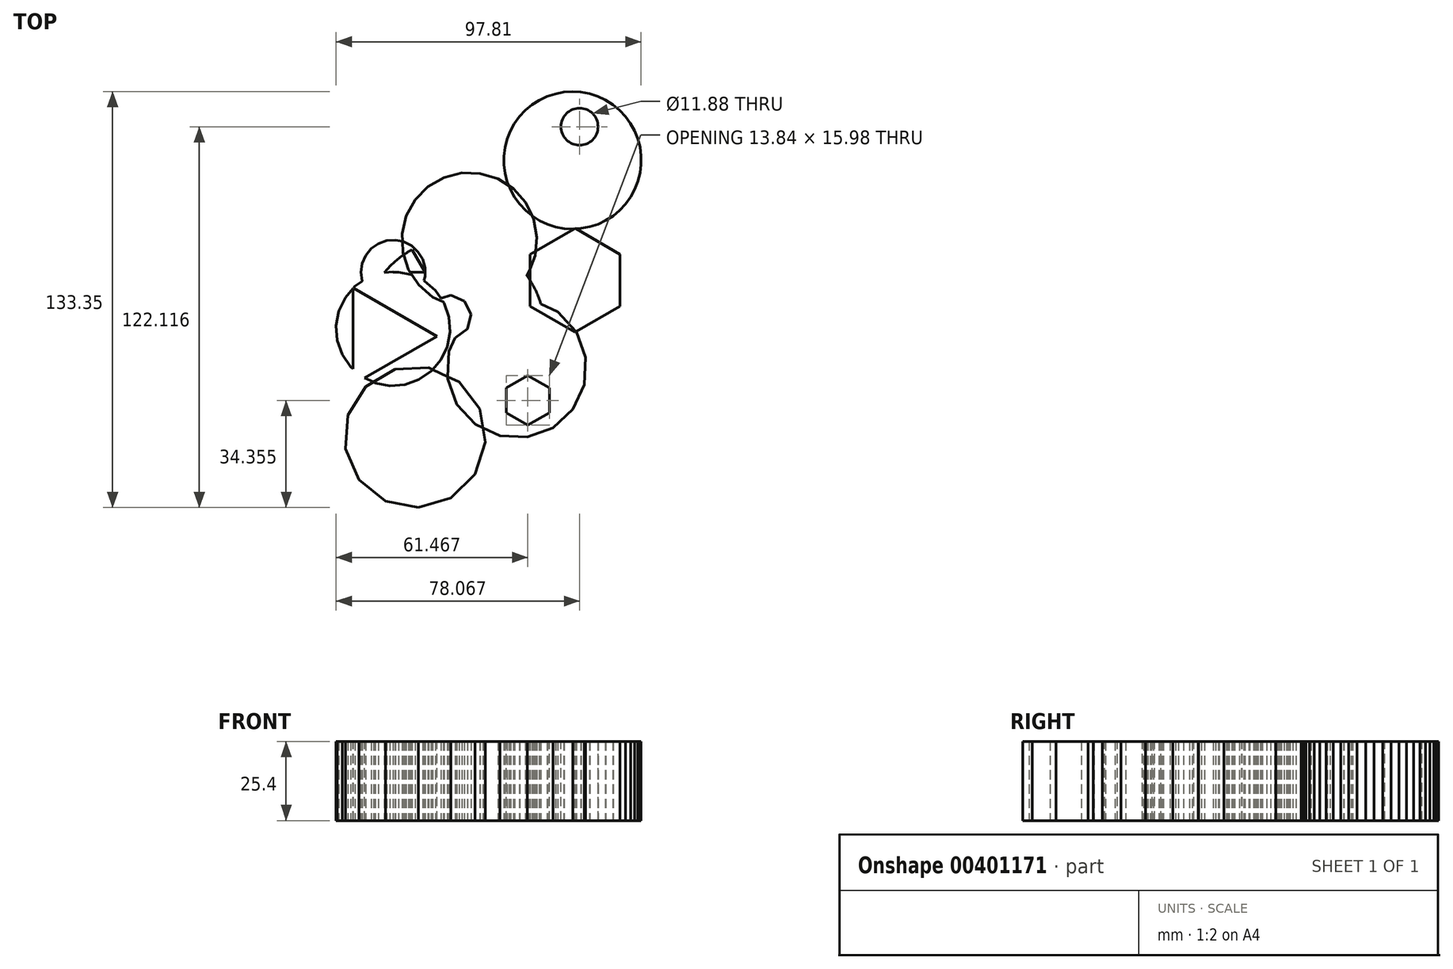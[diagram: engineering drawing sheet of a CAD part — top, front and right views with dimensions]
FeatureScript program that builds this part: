
annotation { "Feature Type Name" : "Feature", "Feature Type Description" : "" }
export const myFeature = defineFeature(function(context is Context, id is Id, definition is map)
    precondition{}
    {
        {
            var Q0;
            Q0=qCreatedBy(makeId("Top.planeOp"),FACE);
            var sketch = newSketch(context, id + "F0", { "sketchPlane" : qUnion([Q0])});
            skCircle(sketch, "E0", {"center": v(0, 0) * mm, "radius": 28.78 * mm});
            skCircle(sketch, "E1.cCircle", {"center": v(-14.58, 21.09) * mm, "radius": 2.96 * mm, "construction": true});
            skLineSegment(sketch, "E1.0", {"start": v(-9.46, 18.13) * mm, "end": v(-19.7, 18.13) * mm});
            skLineSegment(sketch, "E1.1", {"start": v(-19.7, 18.13) * mm, "end": v(-14.58, 27) * mm});
            skLineSegment(sketch, "E1.2", {"start": v(-14.58, 27) * mm, "end": v(-9.46, 18.13) * mm});
            skPoint(sketch, "E1.0.midPoint", {"position": v(-14.58, 18.13) * mm});
            skCircle(sketch, "E2.cCircle", {"center": v(-19.7, 18.13) * mm, "radius": 10.24 * mm, "construction": true});
            skLineSegment(sketch, "E2.0", {"start": v(-9.46, 19.54) * mm, "end": v(-9.46, 16.72) * mm});
            skLineSegment(sketch, "E2.1", {"start": v(-9.46, 16.72) * mm, "end": v(-10.22, 14.01) * mm});
            skLineSegment(sketch, "E2.2", {"start": v(-10.22, 14.01) * mm, "end": v(-11.69, 11.6) * mm});
            skLineSegment(sketch, "E2.3", {"start": v(-11.69, 11.6) * mm, "end": v(-13.74, 9.69) * mm});
            skLineSegment(sketch, "E2.4", {"start": v(-13.74, 9.69) * mm, "end": v(-16.24, 8.4) * mm});
            skLineSegment(sketch, "E2.5", {"start": v(-16.24, 8.4) * mm, "end": v(-19, 7.82) * mm});
            skLineSegment(sketch, "E2.6", {"start": v(-19, 7.82) * mm, "end": v(-21.8, 8.01) * mm});
            skLineSegment(sketch, "E2.7", {"start": v(-21.8, 8.01) * mm, "end": v(-24.46, 8.95) * mm});
            skLineSegment(sketch, "E2.8", {"start": v(-24.46, 8.95) * mm, "end": v(-26.76, 10.58) * mm});
            skLineSegment(sketch, "E2.9", {"start": v(-26.76, 10.58) * mm, "end": v(-28.53, 12.76) * mm});
            skLineSegment(sketch, "E2.10", {"start": v(-28.53, 12.76) * mm, "end": v(-29.66, 15.34) * mm});
            skLineSegment(sketch, "E2.11", {"start": v(-29.66, 15.34) * mm, "end": v(-30.04, 18.13) * mm});
            skLineSegment(sketch, "E2.12", {"start": v(-30.04, 18.13) * mm, "end": v(-29.66, 20.92) * mm});
            skLineSegment(sketch, "E2.13", {"start": v(-29.66, 20.92) * mm, "end": v(-28.53, 23.5) * mm});
            skLineSegment(sketch, "E2.14", {"start": v(-28.53, 23.5) * mm, "end": v(-26.76, 25.68) * mm});
            skLineSegment(sketch, "E2.15", {"start": v(-26.76, 25.68) * mm, "end": v(-24.46, 27.3) * mm});
            skLineSegment(sketch, "E2.16", {"start": v(-24.46, 27.3) * mm, "end": v(-21.8, 28.25) * mm});
            skLineSegment(sketch, "E2.17", {"start": v(-21.8, 28.25) * mm, "end": v(-19, 28.44) * mm});
            skLineSegment(sketch, "E2.18", {"start": v(-19, 28.44) * mm, "end": v(-16.24, 27.87) * mm});
            skLineSegment(sketch, "E2.19", {"start": v(-16.24, 27.87) * mm, "end": v(-13.74, 26.57) * mm});
            skLineSegment(sketch, "E2.20", {"start": v(-13.74, 26.57) * mm, "end": v(-11.69, 24.65) * mm});
            skLineSegment(sketch, "E2.21", {"start": v(-11.69, 24.65) * mm, "end": v(-10.22, 22.25) * mm});
            skLineSegment(sketch, "E2.22", {"start": v(-10.22, 22.25) * mm, "end": v(-9.46, 19.54) * mm});
            skPoint(sketch, "E2.0.midPoint", {"position": v(-9.46, 18.13) * mm});
            skCircle(sketch, "E3.cCircle", {"center": v(4.75, 28.39) * mm, "radius": 21.48 * mm, "construction": true});
            skLineSegment(sketch, "E3.0", {"start": v(15.55, 9.58) * mm, "end": v(10.07, 7.37) * mm});
            skLineSegment(sketch, "E3.1", {"start": v(10.07, 7.37) * mm, "end": v(4.2, 6.71) * mm});
            skLineSegment(sketch, "E3.2", {"start": v(4.2, 6.71) * mm, "end": v(-1.62, 7.66) * mm});
            skLineSegment(sketch, "E3.3", {"start": v(-1.62, 7.66) * mm, "end": v(-6.98, 10.15) * mm});
            skLineSegment(sketch, "E3.4", {"start": v(-6.98, 10.15) * mm, "end": v(-11.46, 14) * mm});
            skLineSegment(sketch, "E3.5", {"start": v(-11.46, 14) * mm, "end": v(-14.74, 18.9) * mm});
            skLineSegment(sketch, "E3.6", {"start": v(-14.74, 18.9) * mm, "end": v(-16.58, 24.52) * mm});
            skLineSegment(sketch, "E3.7", {"start": v(-16.58, 24.52) * mm, "end": v(-16.83, 30.42) * mm});
            skLineSegment(sketch, "E3.8", {"start": v(-16.83, 30.42) * mm, "end": v(-15.49, 36.17) * mm});
            skLineSegment(sketch, "E3.9", {"start": v(-15.49, 36.17) * mm, "end": v(-12.64, 41.34) * mm});
            skLineSegment(sketch, "E3.10", {"start": v(-12.64, 41.34) * mm, "end": v(-8.5, 45.55) * mm});
            skLineSegment(sketch, "E3.11", {"start": v(-8.5, 45.55) * mm, "end": v(-3.38, 48.49) * mm});
            skLineSegment(sketch, "E3.12", {"start": v(-3.38, 48.49) * mm, "end": v(2.35, 49.94) * mm});
            skLineSegment(sketch, "E3.13", {"start": v(2.35, 49.94) * mm, "end": v(8.25, 49.79) * mm});
            skLineSegment(sketch, "E3.14", {"start": v(8.25, 49.79) * mm, "end": v(13.9, 48.05) * mm});
            skLineSegment(sketch, "E3.15", {"start": v(13.9, 48.05) * mm, "end": v(18.86, 44.85) * mm});
            skLineSegment(sketch, "E3.16", {"start": v(18.86, 44.85) * mm, "end": v(22.78, 40.44) * mm});
            skLineSegment(sketch, "E3.17", {"start": v(22.78, 40.44) * mm, "end": v(25.36, 35.13) * mm});
            skLineSegment(sketch, "E3.18", {"start": v(25.36, 35.13) * mm, "end": v(26.42, 29.32) * mm});
            skLineSegment(sketch, "E3.19", {"start": v(26.42, 29.32) * mm, "end": v(25.87, 23.44) * mm});
            skLineSegment(sketch, "E3.20", {"start": v(25.87, 23.44) * mm, "end": v(23.75, 17.93) * mm});
            skLineSegment(sketch, "E3.21", {"start": v(23.75, 17.93) * mm, "end": v(20.22, 13.2) * mm});
            skLineSegment(sketch, "E3.22", {"start": v(20.22, 13.2) * mm, "end": v(15.55, 9.58) * mm});
            skPoint(sketch, "E3.0.midPoint", {"position": v(12.8, 8.47) * mm});
            skCircle(sketch, "E4.cCircle", {"center": v(-19.7, 0) * mm, "radius": 18.14 * mm, "construction": true});
            skLineSegment(sketch, "E4.0", {"start": v(-7.5, -13.63) * mm, "end": v(-11.43, -16.33) * mm});
            skLineSegment(sketch, "E4.1", {"start": v(-11.43, -16.33) * mm, "end": v(-15.94, -17.9) * mm});
            skLineSegment(sketch, "E4.2", {"start": v(-15.94, -17.9) * mm, "end": v(-20.7, -18.27) * mm});
            skLineSegment(sketch, "E4.3", {"start": v(-20.7, -18.27) * mm, "end": v(-25.4, -17.4) * mm});
            skLineSegment(sketch, "E4.4", {"start": v(-25.4, -17.4) * mm, "end": v(-29.7, -15.32) * mm});
            skLineSegment(sketch, "E4.5", {"start": v(-29.7, -15.32) * mm, "end": v(-33.33, -12.21) * mm});
            skLineSegment(sketch, "E4.6", {"start": v(-33.33, -12.21) * mm, "end": v(-36.03, -8.27) * mm});
            skLineSegment(sketch, "E4.7", {"start": v(-36.03, -8.27) * mm, "end": v(-37.61, -3.76) * mm});
            skLineSegment(sketch, "E4.8", {"start": v(-37.61, -3.76) * mm, "end": v(-37.98, 1) * mm});
            skLineSegment(sketch, "E4.9", {"start": v(-37.98, 1) * mm, "end": v(-37.1, 5.7) * mm});
            skLineSegment(sketch, "E4.10", {"start": v(-37.1, 5.7) * mm, "end": v(-35.03, 10) * mm});
            skLineSegment(sketch, "E4.11", {"start": v(-35.03, 10) * mm, "end": v(-31.91, 13.63) * mm});
            skLineSegment(sketch, "E4.12", {"start": v(-31.91, 13.63) * mm, "end": v(-27.97, 16.33) * mm});
            skLineSegment(sketch, "E4.13", {"start": v(-27.97, 16.33) * mm, "end": v(-23.46, 17.9) * mm});
            skLineSegment(sketch, "E4.14", {"start": v(-23.46, 17.9) * mm, "end": v(-18.7, 18.27) * mm});
            skLineSegment(sketch, "E4.15", {"start": v(-18.7, 18.27) * mm, "end": v(-14, 17.4) * mm});
            skLineSegment(sketch, "E4.16", {"start": v(-14, 17.4) * mm, "end": v(-9.7, 15.32) * mm});
            skLineSegment(sketch, "E4.17", {"start": v(-9.7, 15.32) * mm, "end": v(-6.07, 12.21) * mm});
            skLineSegment(sketch, "E4.18", {"start": v(-6.07, 12.21) * mm, "end": v(-3.38, 8.27) * mm});
            skLineSegment(sketch, "E4.19", {"start": v(-3.38, 8.27) * mm, "end": v(-1.8, 3.76) * mm});
            skLineSegment(sketch, "E4.20", {"start": v(-1.8, 3.76) * mm, "end": v(-1.43, -1) * mm});
            skLineSegment(sketch, "E4.21", {"start": v(-1.43, -1) * mm, "end": v(-2.31, -5.7) * mm});
            skLineSegment(sketch, "E4.22", {"start": v(-2.31, -5.7) * mm, "end": v(-4.38, -10) * mm});
            skLineSegment(sketch, "E4.23", {"start": v(-4.38, -10) * mm, "end": v(-7.5, -13.63) * mm});
            skPoint(sketch, "E4.0.midPoint", {"position": v(-9.46, -14.98) * mm});
            skCircle(sketch, "E5.cCircle", {"center": v(19.9, -12.61) * mm, "radius": 21.95 * mm, "construction": true});
            skPoint(sketch, "E5.cCircle.perimeterSnap0", {"position": v(-1.87, -3.35) * mm});
            skLineSegment(sketch, "E5.0", {"start": v(-1.84, -7.3) * mm, "end": v(1.84, 0.6) * mm});
            skLineSegment(sketch, "E5.1", {"start": v(1.84, 0.6) * mm, "end": v(8.28, 6.51) * mm});
            skLineSegment(sketch, "E5.2", {"start": v(8.28, 6.51) * mm, "end": v(16.48, 9.5) * mm});
            skLineSegment(sketch, "E5.3", {"start": v(16.48, 9.5) * mm, "end": v(25.2, 9.13) * mm});
            skLineSegment(sketch, "E5.4", {"start": v(25.2, 9.13) * mm, "end": v(33.13, 5.45) * mm});
            skLineSegment(sketch, "E5.5", {"start": v(33.13, 5.45) * mm, "end": v(39.03, -0.99) * mm});
            skLineSegment(sketch, "E5.6", {"start": v(39.03, -0.99) * mm, "end": v(42.02, -9.2) * mm});
            skLineSegment(sketch, "E5.7", {"start": v(42.02, -9.2) * mm, "end": v(41.65, -17.92) * mm});
            skLineSegment(sketch, "E5.8", {"start": v(41.65, -17.92) * mm, "end": v(37.97, -25.83) * mm});
            skLineSegment(sketch, "E5.9", {"start": v(37.97, -25.83) * mm, "end": v(31.53, -31.74) * mm});
            skLineSegment(sketch, "E5.10", {"start": v(31.53, -31.74) * mm, "end": v(23.33, -34.73) * mm});
            skLineSegment(sketch, "E5.11", {"start": v(23.33, -34.73) * mm, "end": v(14.6, -34.36) * mm});
            skLineSegment(sketch, "E5.12", {"start": v(14.6, -34.36) * mm, "end": v(6.68, -30.67) * mm});
            skLineSegment(sketch, "E5.13", {"start": v(6.68, -30.67) * mm, "end": v(0.78, -24.24) * mm});
            skLineSegment(sketch, "E5.14", {"start": v(0.78, -24.24) * mm, "end": v(-2.22, -16.03) * mm});
            skLineSegment(sketch, "E5.15", {"start": v(-2.22, -16.03) * mm, "end": v(-1.84, -7.3) * mm});
            skPoint(sketch, "E5.0.midPoint", {"position": v(0, -3.35) * mm});
            skPoint(sketch, "E5.0.midPoint.positionSnap0", {"position": v(-1.87, -3.35) * mm});
            skCircle(sketch, "E6.cCircle", {"center": v(-1.62, 3.76) * mm, "radius": 6.53 * mm, "construction": true});
            skLineSegment(sketch, "E6.0", {"start": v(3.13, 8.83) * mm, "end": v(5.28, 4.6) * mm});
            skLineSegment(sketch, "E6.1", {"start": v(5.28, 4.6) * mm, "end": v(4.2, -0.04) * mm});
            skLineSegment(sketch, "E6.2", {"start": v(4.2, -0.04) * mm, "end": v(0.4, -2.9) * mm});
            skLineSegment(sketch, "E6.3", {"start": v(0.4, -2.9) * mm, "end": v(-4.36, -2.63) * mm});
            skLineSegment(sketch, "E6.4", {"start": v(-4.36, -2.63) * mm, "end": v(-7.83, 0.62) * mm});
            skLineSegment(sketch, "E6.5", {"start": v(-7.83, 0.62) * mm, "end": v(-8.4, 5.34) * mm});
            skLineSegment(sketch, "E6.6", {"start": v(-8.4, 5.34) * mm, "end": v(-5.8, 9.32) * mm});
            skLineSegment(sketch, "E6.7", {"start": v(-5.8, 9.32) * mm, "end": v(-1.24, 10.7) * mm});
            skLineSegment(sketch, "E6.8", {"start": v(-1.24, 10.7) * mm, "end": v(3.13, 8.83) * mm});
            skPoint(sketch, "E6.0.midPoint", {"position": v(4.2, 6.71) * mm});
            skCircle(sketch, "E7.cCircle", {"center": v(38.63, 15.56) * mm, "radius": 14.4 * mm, "construction": true});
            skPoint(sketch, "E7.cCircle.centerSnap0", {"position": v(21.98, 15.56) * mm});
            skLineSegment(sketch, "E7.0", {"start": v(24.22, 7.24) * mm, "end": v(24.22, 23.88) * mm});
            skLineSegment(sketch, "E7.1", {"start": v(24.22, 23.88) * mm, "end": v(38.63, 32.2) * mm});
            skLineSegment(sketch, "E7.2", {"start": v(38.63, 32.2) * mm, "end": v(53.04, 23.88) * mm});
            skLineSegment(sketch, "E7.3", {"start": v(53.04, 23.88) * mm, "end": v(53.04, 7.24) * mm});
            skLineSegment(sketch, "E7.4", {"start": v(53.04, 7.24) * mm, "end": v(38.63, -1.08) * mm});
            skLineSegment(sketch, "E7.5", {"start": v(38.63, -1.08) * mm, "end": v(24.22, 7.24) * mm});
            skPoint(sketch, "E7.0.midPoint", {"position": v(24.22, 15.56) * mm});
            skCircle(sketch, "E8.cCircle", {"center": v(37.84, 54) * mm, "radius": 21.98 * mm, "construction": true});
            skLineSegment(sketch, "E8.0", {"start": v(35.14, 32.14) * mm, "end": v(32.42, 32.65) * mm});
            skLineSegment(sketch, "E8.1", {"start": v(32.42, 32.65) * mm, "end": v(29.79, 33.5) * mm});
            skLineSegment(sketch, "E8.2", {"start": v(29.79, 33.5) * mm, "end": v(27.28, 34.66) * mm});
            skLineSegment(sketch, "E8.3", {"start": v(27.28, 34.66) * mm, "end": v(24.94, 36.14) * mm});
            skLineSegment(sketch, "E8.4", {"start": v(24.94, 36.14) * mm, "end": v(22.8, 37.9) * mm});
            skLineSegment(sketch, "E8.5", {"start": v(22.8, 37.9) * mm, "end": v(20.9, 39.9) * mm});
            skLineSegment(sketch, "E8.6", {"start": v(20.9, 39.9) * mm, "end": v(19.27, 42.14) * mm});
            skLineSegment(sketch, "E8.7", {"start": v(19.27, 42.14) * mm, "end": v(17.93, 44.56) * mm});
            skLineSegment(sketch, "E8.8", {"start": v(17.93, 44.56) * mm, "end": v(16.9, 47.13) * mm});
            skLineSegment(sketch, "E8.9", {"start": v(16.9, 47.13) * mm, "end": v(16.21, 49.8) * mm});
            skLineSegment(sketch, "E8.10", {"start": v(16.21, 49.8) * mm, "end": v(15.86, 52.55) * mm});
            skLineSegment(sketch, "E8.11", {"start": v(15.86, 52.55) * mm, "end": v(15.85, 55.32) * mm});
            skLineSegment(sketch, "E8.12", {"start": v(15.85, 55.32) * mm, "end": v(16.19, 58.06) * mm});
            skLineSegment(sketch, "E8.13", {"start": v(16.19, 58.06) * mm, "end": v(16.87, 60.75) * mm});
            skLineSegment(sketch, "E8.14", {"start": v(16.87, 60.75) * mm, "end": v(17.88, 63.32) * mm});
            skLineSegment(sketch, "E8.15", {"start": v(17.88, 63.32) * mm, "end": v(19.2, 65.75) * mm});
            skLineSegment(sketch, "E8.16", {"start": v(19.2, 65.75) * mm, "end": v(20.83, 68) * mm});
            skLineSegment(sketch, "E8.17", {"start": v(20.83, 68) * mm, "end": v(22.71, 70.01) * mm});
            skLineSegment(sketch, "E8.18", {"start": v(22.71, 70.01) * mm, "end": v(24.84, 71.78) * mm});
            skLineSegment(sketch, "E8.19", {"start": v(24.84, 71.78) * mm, "end": v(27.17, 73.27) * mm});
            skLineSegment(sketch, "E8.20", {"start": v(27.17, 73.27) * mm, "end": v(29.67, 74.46) * mm});
            skLineSegment(sketch, "E8.21", {"start": v(29.67, 74.46) * mm, "end": v(32.3, 75.32) * mm});
            skLineSegment(sketch, "E8.22", {"start": v(32.3, 75.32) * mm, "end": v(35.02, 75.84) * mm});
            skLineSegment(sketch, "E8.23", {"start": v(35.02, 75.84) * mm, "end": v(37.78, 76.02) * mm});
            skLineSegment(sketch, "E8.24", {"start": v(37.78, 76.02) * mm, "end": v(40.54, 75.86) * mm});
            skLineSegment(sketch, "E8.25", {"start": v(40.54, 75.86) * mm, "end": v(43.26, 75.35) * mm});
            skLineSegment(sketch, "E8.26", {"start": v(43.26, 75.35) * mm, "end": v(45.89, 74.5) * mm});
            skLineSegment(sketch, "E8.27", {"start": v(45.89, 74.5) * mm, "end": v(48.4, 73.33) * mm});
            skLineSegment(sketch, "E8.28", {"start": v(48.4, 73.33) * mm, "end": v(50.73, 71.85) * mm});
            skLineSegment(sketch, "E8.29", {"start": v(50.73, 71.85) * mm, "end": v(52.87, 70.1) * mm});
            skLineSegment(sketch, "E8.30", {"start": v(52.87, 70.1) * mm, "end": v(54.77, 68.09) * mm});
            skLineSegment(sketch, "E8.31", {"start": v(54.77, 68.09) * mm, "end": v(56.4, 65.85) * mm});
            skLineSegment(sketch, "E8.32", {"start": v(56.4, 65.85) * mm, "end": v(57.74, 63.43) * mm});
            skLineSegment(sketch, "E8.33", {"start": v(57.74, 63.43) * mm, "end": v(58.77, 60.86) * mm});
            skLineSegment(sketch, "E8.34", {"start": v(58.77, 60.86) * mm, "end": v(59.46, 58.19) * mm});
            skLineSegment(sketch, "E8.35", {"start": v(59.46, 58.19) * mm, "end": v(59.82, 55.44) * mm});
            skLineSegment(sketch, "E8.36", {"start": v(59.82, 55.44) * mm, "end": v(59.83, 52.68) * mm});
            skLineSegment(sketch, "E8.37", {"start": v(59.83, 52.68) * mm, "end": v(59.49, 49.93) * mm});
            skLineSegment(sketch, "E8.38", {"start": v(59.49, 49.93) * mm, "end": v(58.8, 47.25) * mm});
            skLineSegment(sketch, "E8.39", {"start": v(58.8, 47.25) * mm, "end": v(57.8, 44.67) * mm});
            skLineSegment(sketch, "E8.40", {"start": v(57.8, 44.67) * mm, "end": v(56.47, 42.25) * mm});
            skLineSegment(sketch, "E8.41", {"start": v(56.47, 42.25) * mm, "end": v(54.85, 40) * mm});
            skLineSegment(sketch, "E8.42", {"start": v(54.85, 40) * mm, "end": v(52.96, 37.98) * mm});
            skLineSegment(sketch, "E8.43", {"start": v(52.96, 37.98) * mm, "end": v(50.83, 36.21) * mm});
            skLineSegment(sketch, "E8.44", {"start": v(50.83, 36.21) * mm, "end": v(48.5, 34.72) * mm});
            skLineSegment(sketch, "E8.45", {"start": v(48.5, 34.72) * mm, "end": v(46, 33.54) * mm});
            skLineSegment(sketch, "E8.46", {"start": v(46, 33.54) * mm, "end": v(43.38, 32.68) * mm});
            skLineSegment(sketch, "E8.47", {"start": v(43.38, 32.68) * mm, "end": v(40.66, 32.15) * mm});
            skLineSegment(sketch, "E8.48", {"start": v(40.66, 32.15) * mm, "end": v(37.9, 31.97) * mm});
            skLineSegment(sketch, "E8.49", {"start": v(37.9, 31.97) * mm, "end": v(35.14, 32.14) * mm});
            skPoint(sketch, "E8.0.midPoint", {"position": v(33.78, 32.4) * mm});
            skCircle(sketch, "E9.cCircle", {"center": v(-12.64, -34.73) * mm, "radius": 21.96 * mm, "construction": true});
            skLineSegment(sketch, "E9.0", {"start": v(-8.29, -12.54) * mm, "end": v(1.53, -17.1) * mm});
            skLineSegment(sketch, "E9.1", {"start": v(1.53, -17.1) * mm, "end": v(8.1, -25.7) * mm});
            skLineSegment(sketch, "E9.2", {"start": v(8.1, -25.7) * mm, "end": v(9.92, -36.38) * mm});
            skLineSegment(sketch, "E9.3", {"start": v(9.92, -36.38) * mm, "end": v(6.58, -46.67) * mm});
            skLineSegment(sketch, "E9.4", {"start": v(6.58, -46.67) * mm, "end": v(-1.17, -54.23) * mm});
            skLineSegment(sketch, "E9.5", {"start": v(-1.17, -54.23) * mm, "end": v(-11.55, -57.33) * mm});
            skLineSegment(sketch, "E9.6", {"start": v(-11.55, -57.33) * mm, "end": v(-22.17, -55.24) * mm});
            skLineSegment(sketch, "E9.7", {"start": v(-22.17, -55.24) * mm, "end": v(-30.61, -48.46) * mm});
            skLineSegment(sketch, "E9.8", {"start": v(-30.61, -48.46) * mm, "end": v(-34.93, -38.54) * mm});
            skLineSegment(sketch, "E9.9", {"start": v(-34.93, -38.54) * mm, "end": v(-34.15, -27.74) * mm});
            skLineSegment(sketch, "E9.10", {"start": v(-34.15, -27.74) * mm, "end": v(-28.43, -18.54) * mm});
            skLineSegment(sketch, "E9.11", {"start": v(-28.43, -18.54) * mm, "end": v(-19.1, -13.06) * mm});
            skLineSegment(sketch, "E9.12", {"start": v(-19.1, -13.06) * mm, "end": v(-8.29, -12.54) * mm});
            skPoint(sketch, "E9.0.midPoint", {"position": v(-3.38, -14.82) * mm});
            skCircle(sketch, "E10.cCircle", {"center": v(41.91, 66.19) * mm, "radius": 4.58 * mm, "construction": true});
            skPoint(sketch, "E10.0.midPoint", {"position": v(45.12, 62.92) * mm});
            skSolve(sketch);
        }
        {
            var Q0;
            {var subQ4=sQuery(id+"F0.wireOp",EDGE,"E3.16");Q0=makeQuery(id+"F0.imprint","IMPRINT",FACE,{"disambiguationData":[TD([[makeQuery(id+"F0.imprint","IMPRINT",EDGE,{"derivedFrom":subQ4}),1.0]])]});}
            var Q1;
            {var subQ6=sQuery(id+"F0.wireOp",EDGE,"E2.21");Q1=makeQuery(id+"F0.imprint","IMPRINT",FACE,{"disambiguationData":[TD([[makeQuery(id+"F0.imprint","IMPRINT",EDGE,{"derivedFrom":subQ6}),1.0]])]});}
            var Q2;
            {var subQ1=sQuery(id+"F0.wireOp",EDGE,"E7.3");Q2=makeQuery(id+"F0.imprint","IMPRINT",FACE,{"disambiguationData":[TD([[makeQuery(id+"F0.imprint","IMPRINT",EDGE,{"derivedFrom":subQ1}),-1.0]])]});}
            var Q3;
            {var subQ21=sQuery(id+"F0.wireOp",EDGE,"E2.19");Q3=makeQuery(id+"F0.imprint","IMPRINT",FACE,{"disambiguationData":[TD([[makeQuery(id+"F0.imprint","IMPRINT",EDGE,{"derivedFrom":subQ21}),1.0]])]});}
            var Q4;
            {var subQ12=sQuery(id+"F0.wireOp",EDGE,"E2.11");Q4=makeQuery(id+"F0.imprint","IMPRINT",FACE,{"disambiguationData":[TD([[makeQuery(id+"F0.imprint","IMPRINT",EDGE,{"derivedFrom":subQ12}),-1.0]])]});}
            var Q5;
            {var subQ5=sQuery(id+"F0.wireOp",EDGE,"E4.5");Q5=makeQuery(id+"F0.imprint","IMPRINT",FACE,{"disambiguationData":[TD([[makeQuery(id+"F0.imprint","IMPRINT",EDGE,{"derivedFrom":subQ5}),-1.0]])]});}
            var Q6;
            {var subQ15=sQuery(id+"F0.wireOp",EDGE,"E2.3");Q6=makeQuery(id+"F0.imprint","IMPRINT",FACE,{"disambiguationData":[TD([[makeQuery(id+"F0.imprint","IMPRINT",EDGE,{"derivedFrom":subQ15}),1.0]])]});}
            var Q7;
            {var subQ6=sQuery(id+"F0.wireOp",EDGE,"E2.3");Q7=makeQuery(id+"F0.imprint","IMPRINT",FACE,{"disambiguationData":[TD([[makeQuery(id+"F0.imprint","IMPRINT",EDGE,{"derivedFrom":subQ6}),-1.0]])]});}
            var Q8;
            {var subQ5=sQuery(id+"F0.wireOp",EDGE,"E1.2");var subQ7=sQuery(id+"F0.wireOp",EDGE,"E0");var subQ8=makeQuery(id+"F0.imprint","INTERSECT",VERTEX,{"derivedFrom":[subQ7,subQ5]});Q8=makeQuery(id+"F0.imprint","IMPRINT",FACE,{"disambiguationData":[TD([[makeQuery(id+"F0.imprint","IMPRINT",EDGE,{"disambiguationData":[TD([[subQ8,-1.0]])],"derivedFrom":subQ7}),1.0]])]});}
            var Q9;
            {var subQ5=sQuery(id+"F0.wireOp",EDGE,"E9.3");Q9=makeQuery(id+"F0.imprint","IMPRINT",FACE,{"disambiguationData":[TD([[makeQuery(id+"F0.imprint","IMPRINT",EDGE,{"derivedFrom":subQ5}),-1.0]])]});}
            var Q10;
            {var subQ12=sQuery(id+"F0.wireOp",EDGE,"E5.6");Q10=makeQuery(id+"F0.imprint","IMPRINT",FACE,{"disambiguationData":[TD([[makeQuery(id+"F0.imprint","IMPRINT",EDGE,{"derivedFrom":subQ12}),-1.0]])]});}
            var Q11;
            {var subQ9=sQuery(id+"F0.wireOp",EDGE,"E4.0");Q11=makeQuery(id+"F0.imprint","IMPRINT",FACE,{"disambiguationData":[TD([[makeQuery(id+"F0.imprint","IMPRINT",EDGE,{"derivedFrom":subQ9}),1.0]])]});}
            var Q12;
            {var subQ11=sQuery(id+"F0.wireOp",EDGE,"E5.2");Q12=makeQuery(id+"F0.imprint","IMPRINT",FACE,{"disambiguationData":[TD([[makeQuery(id+"F0.imprint","IMPRINT",EDGE,{"derivedFrom":subQ11}),-1.0]])]});}
            var Q13;
            {var subQ1=sQuery(id+"F0.wireOp",EDGE,"E4.19");Q13=makeQuery(id+"F0.imprint","IMPRINT",FACE,{"disambiguationData":[TD([[makeQuery(id+"F0.imprint","IMPRINT",EDGE,{"derivedFrom":subQ1}),-1.0]])]});}
            var Q14;
            Q14=makeQuery(id+"F0.imprint","IMPRINT",FACE,{"disambiguationData":[TD([[makeQuery(id+"F0.imprint","IMPRINT",EDGE,{"derivedFrom":sQuery(id+"F0.wireOp",EDGE,"E3.0")}),1.0]])]});
            var Q15;
            {var subQ0=sQuery(id+"F0.wireOp",EDGE,"E4.13");Q15=makeQuery(id+"F0.imprint","IMPRINT",FACE,{"disambiguationData":[TD([[makeQuery(id+"F0.imprint","IMPRINT",EDGE,{"derivedFrom":subQ0}),-1.0]])]});}
            extrude(context, id + "F1", {"entities" : qUnion([Q0, Q1, Q2, Q3, Q4, Q5, Q6, Q7, Q8, Q9, Q10, Q11, Q12, Q13, Q14, Q15]), "depth" : 25.4 * mm});
        }
        {
            var Q0;
            Q0=makeQuery(id+"F1.opExtrude","CAP_FACE",FACE,{"disambiguationData":[OSD([sQuery(id+"F0.wireOp",EDGE,"E3.15"),sQuery(id+"F0.wireOp",EDGE,"E3.16"),sQuery(id+"F0.wireOp",EDGE,"E3.17"),sQuery(id+"F0.wireOp",EDGE,"E7.1"),sQuery(id+"F0.wireOp",EDGE,"E7.2"),sQuery(id+"F0.wireOp",EDGE,"E8.0"),sQuery(id+"F0.wireOp",EDGE,"E8.1"),sQuery(id+"F0.wireOp",EDGE,"E8.2"),sQuery(id+"F0.wireOp",EDGE,"E8.3"),sQuery(id+"F0.wireOp",EDGE,"E8.4"),sQuery(id+"F0.wireOp",EDGE,"E8.8"),sQuery(id+"F0.wireOp",EDGE,"E8.9"),sQuery(id+"F0.wireOp",EDGE,"E8.10"),sQuery(id+"F0.wireOp",EDGE,"E8.11"),sQuery(id+"F0.wireOp",EDGE,"E8.12"),sQuery(id+"F0.wireOp",EDGE,"E8.13"),sQuery(id+"F0.wireOp",EDGE,"E8.14"),sQuery(id+"F0.wireOp",EDGE,"E8.15"),sQuery(id+"F0.wireOp",EDGE,"E8.16"),sQuery(id+"F0.wireOp",EDGE,"E8.17"),sQuery(id+"F0.wireOp",EDGE,"E8.18"),sQuery(id+"F0.wireOp",EDGE,"E8.19"),sQuery(id+"F0.wireOp",EDGE,"E8.20"),sQuery(id+"F0.wireOp",EDGE,"E8.21"),sQuery(id+"F0.wireOp",EDGE,"E8.22"),sQuery(id+"F0.wireOp",EDGE,"E8.23"),sQuery(id+"F0.wireOp",EDGE,"E8.24"),sQuery(id+"F0.wireOp",EDGE,"E8.25"),sQuery(id+"F0.wireOp",EDGE,"E8.26"),sQuery(id+"F0.wireOp",EDGE,"E8.27"),sQuery(id+"F0.wireOp",EDGE,"E8.28"),sQuery(id+"F0.wireOp",EDGE,"E8.29"),sQuery(id+"F0.wireOp",EDGE,"E8.30"),sQuery(id+"F0.wireOp",EDGE,"E8.31"),sQuery(id+"F0.wireOp",EDGE,"E8.32"),sQuery(id+"F0.wireOp",EDGE,"E8.33"),sQuery(id+"F0.wireOp",EDGE,"E8.34"),sQuery(id+"F0.wireOp",EDGE,"E8.35"),sQuery(id+"F0.wireOp",EDGE,"E8.36"),sQuery(id+"F0.wireOp",EDGE,"E8.37"),sQuery(id+"F0.wireOp",EDGE,"E8.38"),sQuery(id+"F0.wireOp",EDGE,"E8.39"),sQuery(id+"F0.wireOp",EDGE,"E8.40"),sQuery(id+"F0.wireOp",EDGE,"E8.41"),sQuery(id+"F0.wireOp",EDGE,"E8.42"),sQuery(id+"F0.wireOp",EDGE,"E8.43"),sQuery(id+"F0.wireOp",EDGE,"E8.44"),sQuery(id+"F0.wireOp",EDGE,"E8.45"),sQuery(id+"F0.wireOp",EDGE,"E8.46"),sQuery(id+"F0.wireOp",EDGE,"E8.47"),sQuery(id+"F0.wireOp",EDGE,"E8.48"),sQuery(id+"F0.wireOp",EDGE,"E8.49")])],"isStart":false});
            var sketch = newSketch(context, id + "F2", { "sketchPlane" : qUnion([Q0])});
            skCircle(sketch, "E11", {"center": v(40.09, 64.79) * mm, "radius": 5.94 * mm});
            skSolve(sketch);
        }
        {
            var Q0;
            Q0 = qSketchRegion(id + "F2", true);
            extrude(context, id + "F3", {"entities" : qUnion([Q0]), "operationType" : NewBodyOperationType.REMOVE, "endBound" : BoundingType.THROUGH_ALL, "oppositeDirection" : true, "depth" : 25.4 * mm});
        }
        {
            var Q0;
            Q0=makeQuery(id+"F1.opExtrude","CAP_FACE",FACE,{"disambiguationData":[OSD([sQuery(id+"F0.wireOp",EDGE,"E0"),sQuery(id+"F0.wireOp",EDGE,"E2.0"),sQuery(id+"F0.wireOp",EDGE,"E2.1"),sQuery(id+"F0.wireOp",EDGE,"E2.18"),sQuery(id+"F0.wireOp",EDGE,"E2.19"),sQuery(id+"F0.wireOp",EDGE,"E2.20"),sQuery(id+"F0.wireOp",EDGE,"E2.21"),sQuery(id+"F0.wireOp",EDGE,"E2.22"),sQuery(id+"F0.wireOp",EDGE,"E3.7"),sQuery(id+"F0.wireOp",EDGE,"E3.8"),sQuery(id+"F0.wireOp",EDGE,"E3.9"),sQuery(id+"F0.wireOp",EDGE,"E3.10"),sQuery(id+"F0.wireOp",EDGE,"E3.11"),sQuery(id+"F0.wireOp",EDGE,"E3.12"),sQuery(id+"F0.wireOp",EDGE,"E3.13"),sQuery(id+"F0.wireOp",EDGE,"E3.14"),sQuery(id+"F0.wireOp",EDGE,"E3.15"),sQuery(id+"F0.wireOp",EDGE,"E3.17"),sQuery(id+"F0.wireOp",EDGE,"E3.18"),sQuery(id+"F0.wireOp",EDGE,"E3.19"),sQuery(id+"F0.wireOp",EDGE,"E3.20"),sQuery(id+"F0.wireOp",EDGE,"E3.21"),sQuery(id+"F0.wireOp",EDGE,"E4.16"),sQuery(id+"F0.wireOp",EDGE,"E4.17"),sQuery(id+"F0.wireOp",EDGE,"E4.18"),sQuery(id+"F0.wireOp",EDGE,"E5.0"),sQuery(id+"F0.wireOp",EDGE,"E5.5"),sQuery(id+"F0.wireOp",EDGE,"E5.6"),sQuery(id+"F0.wireOp",EDGE,"E5.7"),sQuery(id+"F0.wireOp",EDGE,"E5.8"),sQuery(id+"F0.wireOp",EDGE,"E5.9"),sQuery(id+"F0.wireOp",EDGE,"E5.10"),sQuery(id+"F0.wireOp",EDGE,"E5.11"),sQuery(id+"F0.wireOp",EDGE,"E5.12"),sQuery(id+"F0.wireOp",EDGE,"E5.15"),sQuery(id+"F0.wireOp",EDGE,"E6.0"),sQuery(id+"F0.wireOp",EDGE,"E6.1"),sQuery(id+"F0.wireOp",EDGE,"E6.2"),sQuery(id+"F0.wireOp",EDGE,"E6.3"),sQuery(id+"F0.wireOp",EDGE,"E6.7"),sQuery(id+"F0.wireOp",EDGE,"E6.8"),sQuery(id+"F0.wireOp",EDGE,"E7.0"),sQuery(id+"F0.wireOp",EDGE,"E7.1"),sQuery(id+"F0.wireOp",EDGE,"E7.4"),sQuery(id+"F0.wireOp",EDGE,"E7.5"),sQuery(id+"F0.wireOp",EDGE,"E8.4"),sQuery(id+"F0.wireOp",EDGE,"E8.5"),sQuery(id+"F0.wireOp",EDGE,"E8.6"),sQuery(id+"F0.wireOp",EDGE,"E8.7"),sQuery(id+"F0.wireOp",EDGE,"E8.8"),sQuery(id+"F0.wireOp",EDGE,"E9.0"),sQuery(id+"F0.wireOp",EDGE,"E9.1"),sQuery(id+"F0.wireOp",EDGE,"E9.2")])],"isStart":false});
            var sketch = newSketch(context, id + "F4", { "sketchPlane" : qUnion([Q0])});
            skCircle(sketch, "E12.cCircle", {"center": v(23.49, -22.97) * mm, "radius": 6.92 * mm, "construction": true});
            skLineSegment(sketch, "E12.0", {"start": v(30.4, -18.98) * mm, "end": v(30.4, -26.97) * mm});
            skLineSegment(sketch, "E12.1", {"start": v(30.4, -26.97) * mm, "end": v(23.49, -30.96) * mm});
            skLineSegment(sketch, "E12.2", {"start": v(23.49, -30.96) * mm, "end": v(16.57, -26.97) * mm});
            skLineSegment(sketch, "E12.3", {"start": v(16.57, -26.97) * mm, "end": v(16.57, -18.98) * mm});
            skLineSegment(sketch, "E12.4", {"start": v(16.57, -18.98) * mm, "end": v(23.49, -14.99) * mm});
            skLineSegment(sketch, "E12.5", {"start": v(23.49, -14.99) * mm, "end": v(30.4, -18.98) * mm});
            skPoint(sketch, "E12.0.midPoint", {"position": v(30.4, -22.97) * mm});
            skSolve(sketch);
        }
        {
            var Q0;
            Q0 = qSketchRegion(id + "F4", true);
            extrude(context, id + "F5", {"entities" : qUnion([Q0]), "operationType" : NewBodyOperationType.REMOVE, "endBound" : BoundingType.THROUGH_ALL, "oppositeDirection" : true, "depth" : 25.4 * mm});
        }
        {
            var Q0;
            Q0=makeQuery(id+"F1.opExtrude","CAP_FACE",FACE,{"disambiguationData":[OSD([sQuery(id+"F0.wireOp",EDGE,"E0"),sQuery(id+"F0.wireOp",EDGE,"E1.0"),sQuery(id+"F0.wireOp",EDGE,"E1.1"),sQuery(id+"F0.wireOp",EDGE,"E2.10"),sQuery(id+"F0.wireOp",EDGE,"E2.11"),sQuery(id+"F0.wireOp",EDGE,"E2.12"),sQuery(id+"F0.wireOp",EDGE,"E2.13"),sQuery(id+"F0.wireOp",EDGE,"E2.14"),sQuery(id+"F0.wireOp",EDGE,"E2.15"),sQuery(id+"F0.wireOp",EDGE,"E2.16"),sQuery(id+"F0.wireOp",EDGE,"E2.17"),sQuery(id+"F0.wireOp",EDGE,"E2.18"),sQuery(id+"F0.wireOp",EDGE,"E3.3"),sQuery(id+"F0.wireOp",EDGE,"E3.4"),sQuery(id+"F0.wireOp",EDGE,"E3.5"),sQuery(id+"F0.wireOp",EDGE,"E3.6"),sQuery(id+"F0.wireOp",EDGE,"E3.7"),sQuery(id+"F0.wireOp",EDGE,"E4.4"),sQuery(id+"F0.wireOp",EDGE,"E4.5"),sQuery(id+"F0.wireOp",EDGE,"E4.6"),sQuery(id+"F0.wireOp",EDGE,"E4.7"),sQuery(id+"F0.wireOp",EDGE,"E4.8"),sQuery(id+"F0.wireOp",EDGE,"E4.9"),sQuery(id+"F0.wireOp",EDGE,"E4.10"),sQuery(id+"F0.wireOp",EDGE,"E4.11"),sQuery(id+"F0.wireOp",EDGE,"E4.12"),sQuery(id+"F0.wireOp",EDGE,"E4.14"),sQuery(id+"F0.wireOp",EDGE,"E4.15"),sQuery(id+"F0.wireOp",EDGE,"E4.16"),sQuery(id+"F0.wireOp",EDGE,"E4.18"),sQuery(id+"F0.wireOp",EDGE,"E4.19"),sQuery(id+"F0.wireOp",EDGE,"E4.20"),sQuery(id+"F0.wireOp",EDGE,"E4.21"),sQuery(id+"F0.wireOp",EDGE,"E4.22"),sQuery(id+"F0.wireOp",EDGE,"E4.23"),sQuery(id+"F0.wireOp",EDGE,"E9.0"),sQuery(id+"F0.wireOp",EDGE,"E9.11"),sQuery(id+"F0.wireOp",EDGE,"E9.12")])],"isStart":false});
            var sketch = newSketch(context, id + "F6", { "sketchPlane" : qUnion([Q0])});
            skCircle(sketch, "E13.cCircle", {"center": v(-23.57, -2.4) * mm, "radius": 8.95 * mm, "construction": true});
            skLineSegment(sketch, "E13.0", {"start": v(-32.51, -17.9) * mm, "end": v(-32.51, 13.1) * mm});
            skLineSegment(sketch, "E13.1", {"start": v(-32.51, 13.1) * mm, "end": v(-5.67, -2.4) * mm});
            skLineSegment(sketch, "E13.2", {"start": v(-5.67, -2.4) * mm, "end": v(-32.51, -17.9) * mm});
            skPoint(sketch, "E13.0.midPoint", {"position": v(-32.51, -2.4) * mm});
            skSolve(sketch);
        }
        {
            var Q0;
            {var subQ3=sQuery(id+"F0.wireOp",EDGE,"E4.5");var subQ7=sQuery(id+"F6.wireOp",EDGE,"E13.0");var subQ11=makeQuery(id+"F1.opExtrude","CAP_EDGE",EDGE,{"disambiguationData":[OSD([subQ3])],"isStart":false});var subQ13=makeQuery(id+"F6.imprint","INTERSECT",VERTEX,{"derivedFrom":[subQ11,subQ7]});Q0=makeQuery(id+"F6.imprint","IMPRINT",FACE,{"disambiguationData":[TD([[makeQuery(id+"F6.imprint","IMPRINT",EDGE,{"disambiguationData":[TD([[subQ13,-1.0]])],"derivedFrom":subQ7}),-1.0]])]});}
            extrude(context, id + "F7", {"entities" : qUnion([Q0]), "operationType" : NewBodyOperationType.REMOVE, "endBound" : BoundingType.THROUGH_ALL, "oppositeDirection" : true, "depth" : 25.4 * mm});
        }
    });
